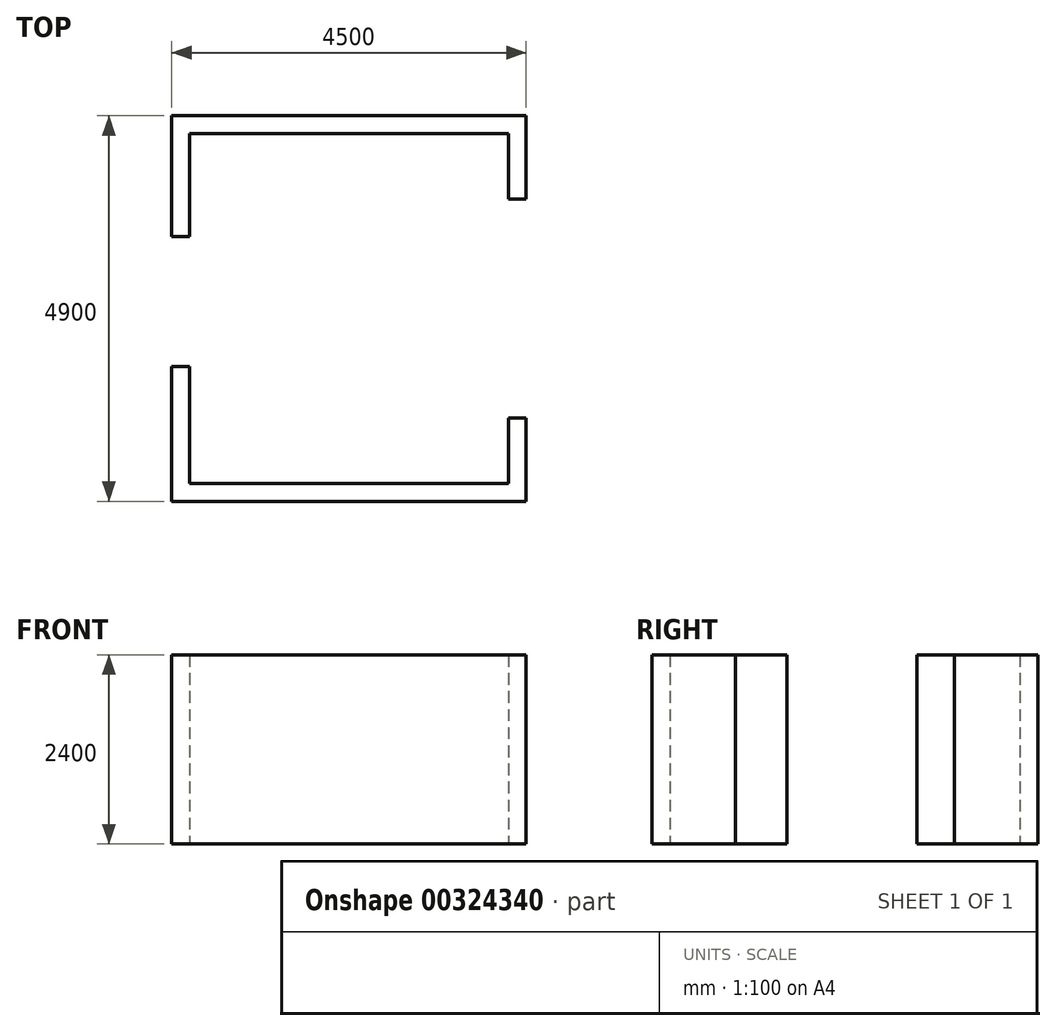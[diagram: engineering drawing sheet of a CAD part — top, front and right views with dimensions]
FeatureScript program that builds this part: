
annotation { "Feature Type Name" : "Feature", "Feature Type Description" : "" }
export const myFeature = defineFeature(function(context is Context, id is Id, definition is map)
    precondition{}
    {
        {
            var Q0;
            Q0=qCreatedBy(makeId("Top.planeOp"),FACE);
            var sketch = newSketch(context, id + "F0", { "sketchPlane" : qUnion([Q0])});
            skLineSegment(sketch, "E0.bottom", {"start": v(2250, -2450) * mm, "end": v(-2250, -2450) * mm});
            skLineSegment(sketch, "E0.top", {"start": v(2250, 2450) * mm, "end": v(-2250, 2450) * mm});
            skLineSegment(sketch, "E0.left", {"start": v(2250, -2450) * mm, "end": v(2250, -1390) * mm});
            skLineSegment(sketch, "E0.right", {"start": v(-2250, -2450) * mm, "end": v(-2250, 2450) * mm});
            skPoint(sketch, "E0.middle", {"position": v(0, 0) * mm});
            skLineSegment(sketch, "E1.0", {"start": v(2025, 2225) * mm, "end": v(-2025, 2225) * mm});
            skLineSegment(sketch, "E1.1", {"start": v(2025, -2225) * mm, "end": v(2025, -1390) * mm});
            skLineSegment(sketch, "E1.2", {"start": v(2025, -2225) * mm, "end": v(-2025, -2225) * mm});
            skLineSegment(sketch, "E1.3", {"start": v(-2025, -2225) * mm, "end": v(-2025, 2225) * mm});
            skLineSegment(sketch, "E2", {"start": v(2025, 1390) * mm, "end": v(2250, 1390) * mm});
            skLineSegment(sketch, "E3", {"start": v(2025, -1390) * mm, "end": v(2250, -1390) * mm});
            skLineSegment(sketch, "E4.trimOffspring", {"start": v(2025, 1390) * mm, "end": v(2025, 2225) * mm});
            skLineSegment(sketch, "E5.trimOffspring", {"start": v(2250, 1390) * mm, "end": v(2250, 2450) * mm});
            skSolve(sketch);
        }
        {
            var Q0;
            Q0=makeQuery(id+"F0.imprint","IMPRINT",FACE,{"disambiguationData":[TD([[makeQuery(id+"F0.imprint","IMPRINT",EDGE,{"derivedFrom":sQuery(id+"F0.wireOp",EDGE,"E0.bottom")}),-1.0]])]});
            extrude(context, id + "F1", {"entities" : qUnion([Q0]), "depth" : 2400 * mm});
        }
        {
            var Q0;
            Q0=makeQuery(id+"F1.opExtrude","CAP_FACE",FACE,{"disambiguationData":[OSD([sQuery(id+"F0.wireOp",EDGE,"E0.bottom"),sQuery(id+"F0.wireOp",EDGE,"E0.top"),sQuery(id+"F0.wireOp",EDGE,"E0.left"),sQuery(id+"F0.wireOp",EDGE,"E0.right"),sQuery(id+"F0.wireOp",EDGE,"E1.0"),sQuery(id+"F0.wireOp",EDGE,"E1.1"),sQuery(id+"F0.wireOp",EDGE,"E1.2"),sQuery(id+"F0.wireOp",EDGE,"E1.3"),sQuery(id+"F0.wireOp",EDGE,"E2"),sQuery(id+"F0.wireOp",EDGE,"E3"),sQuery(id+"F0.wireOp",EDGE,"E4.trimOffspring"),sQuery(id+"F0.wireOp",EDGE,"E5.trimOffspring")])],"isStart":false});
            cPlane(context, id + "F2", {"entities" : qUnion([Q0]), "cplaneType" : CPlaneType.OFFSET, "offset" : 200 * mm, "width" : 150 * mm, "height" : 150 * mm});
        }
        {
            var Q0;
            Q0=qCreatedBy(id+"F2.planeOp",FACE);
            var sketch = newSketch(context, id + "F3", { "sketchPlane" : qUnion([Q0])});
            skLineSegment(sketch, "E6.0", {"start": v(-2025, -2225) * mm, "end": v(-2025, 2225) * mm});
            skLineSegment(sketch, "E7.0.0", {"start": v(2025, 2225) * mm, "end": v(2025, 1390) * mm});
            skLineSegment(sketch, "E7.0.1", {"start": v(2025, 1390) * mm, "end": v(2250, 1390) * mm});
            skLineSegment(sketch, "E7.0.2", {"start": v(2250, 1390) * mm, "end": v(2250, 2450) * mm});
            skLineSegment(sketch, "E7.0.3", {"start": v(2250, 2450) * mm, "end": v(-2250, 2450) * mm});
            skLineSegment(sketch, "E7.0.4", {"start": v(-2250, 2450) * mm, "end": v(-2250, -2450) * mm});
            skLineSegment(sketch, "E7.0.5", {"start": v(-2250, -2450) * mm, "end": v(2250, -2450) * mm});
            skLineSegment(sketch, "E7.0.6", {"start": v(2250, -2450) * mm, "end": v(2250, -1390) * mm});
            skLineSegment(sketch, "E7.0.7", {"start": v(2250, -1390) * mm, "end": v(2025, -1390) * mm});
            skLineSegment(sketch, "E7.0.8", {"start": v(2025, -1390) * mm, "end": v(2025, -2225) * mm});
            skLineSegment(sketch, "E7.0.9", {"start": v(2025, -2225) * mm, "end": v(-2025, -2225) * mm});
            skLineSegment(sketch, "E7.0.11", {"start": v(-2025, 2225) * mm, "end": v(2025, 2225) * mm});
            skPoint(sketch, "E8", {"position": v(0, 0) * mm});
            skPoint(sketch, "E8.positionSnap0", {"position": v(-2025, 0) * mm});
            skPoint(sketch, "E8.positionSnap1", {"position": v(0, 2225) * mm});
            skSolve(sketch);
        }
        {
            var Q0;
            Q0=makeQuery(id+"F1.opExtrude","CAP_FACE",FACE,{"disambiguationData":[OSD([sQuery(id+"F0.wireOp",EDGE,"E0.bottom"),sQuery(id+"F0.wireOp",EDGE,"E0.top"),sQuery(id+"F0.wireOp",EDGE,"E0.left"),sQuery(id+"F0.wireOp",EDGE,"E0.right"),sQuery(id+"F0.wireOp",EDGE,"E1.0"),sQuery(id+"F0.wireOp",EDGE,"E1.1"),sQuery(id+"F0.wireOp",EDGE,"E1.2"),sQuery(id+"F0.wireOp",EDGE,"E1.3"),sQuery(id+"F0.wireOp",EDGE,"E2"),sQuery(id+"F0.wireOp",EDGE,"E3"),sQuery(id+"F0.wireOp",EDGE,"E4.trimOffspring"),sQuery(id+"F0.wireOp",EDGE,"E5.trimOffspring")])],"isStart":false});
            var sketch = newSketch(context, id + "F4", { "sketchPlane" : qUnion([Q0])});
            skLineSegment(sketch, "E9.bottom", {"start": v(-1001.08, 911.94) * mm, "end": v(-3791.76, 911.94) * mm});
            skLineSegment(sketch, "E9.top", {"start": v(-1001.08, -733.67) * mm, "end": v(-3791.76, -733.67) * mm});
            skLineSegment(sketch, "E9.left", {"start": v(-1001.08, 911.94) * mm, "end": v(-1001.08, -733.67) * mm});
            skLineSegment(sketch, "E9.right", {"start": v(-3791.76, 911.94) * mm, "end": v(-3791.76, -733.67) * mm});
            skSolve(sketch);
        }
        {
            var Q0;
            {var subQ0=sQuery(id+"F4.wireOp",EDGE,"E9.left");Q0=makeQuery(id+"F4.imprint","IMPRINT",FACE,{"disambiguationData":[TD([[makeQuery(id+"F4.imprint","IMPRINT",EDGE,{"derivedFrom":subQ0}),-1.0]])]});}
            var Q1;
            {var subQ0=sQuery(id+"F4.wireOp",EDGE,"E9.right");Q1=makeQuery(id+"F4.imprint","IMPRINT",FACE,{"disambiguationData":[TD([[makeQuery(id+"F4.imprint","IMPRINT",EDGE,{"derivedFrom":subQ0}),1.0]])]});}
            var Q2;
            {var subQ0=sQuery(id+"F4.wireOp",EDGE,"E9.bottom");var subQ1=makeQuery(id+"F1.opExtrude","CAP_EDGE",EDGE,{"disambiguationData":[OSD([sQuery(id+"F0.wireOp",EDGE,"E1.3")])],"isStart":false});var subQ2=makeQuery(id+"F4.imprint","INTERSECT",VERTEX,{"derivedFrom":[subQ1,subQ0]});Q2=makeQuery(id+"F4.imprint","IMPRINT",FACE,{"disambiguationData":[TD([[makeQuery(id+"F4.imprint","IMPRINT",EDGE,{"disambiguationData":[TD([[subQ2,-1.0]])],"derivedFrom":subQ0}),1.0]])]});}
            extrude(context, id + "F5", {"entities" : qUnion([Q0, Q1, Q2]), "operationType" : NewBodyOperationType.REMOVE, "endBound" : BoundingType.THROUGH_ALL, "oppositeDirection" : true, "depth" : 25 * mm});
        }
    });
